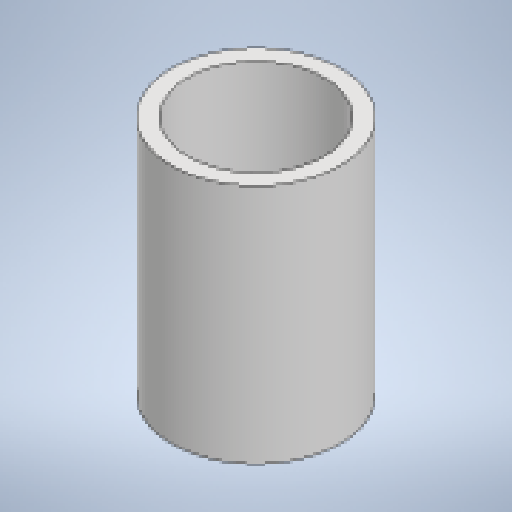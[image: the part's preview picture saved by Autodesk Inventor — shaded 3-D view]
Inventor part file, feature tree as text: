
AUTODESK INVENTOR PART (.ipt)
format: ipt  version: 2025.1 (Build 291241020, 241B)  size: 166,400 bytes
history: native  units: mm
features: extrude x1, sketch x1
ambient origin geometry x8: Origin, YZ Plane, XZ Plane, XY Plane, X Axis, Y Axis, Z Axis, Center Point
bodies: Body1 (feature_tree)
feature tree (2):
  extrude  "Extrusion5"  Depth=30.0mm
  sketch  "Sketch11"  dims[d187=21.0mm d188=2.0mm d189=30.0mm d190=0.0mm]
